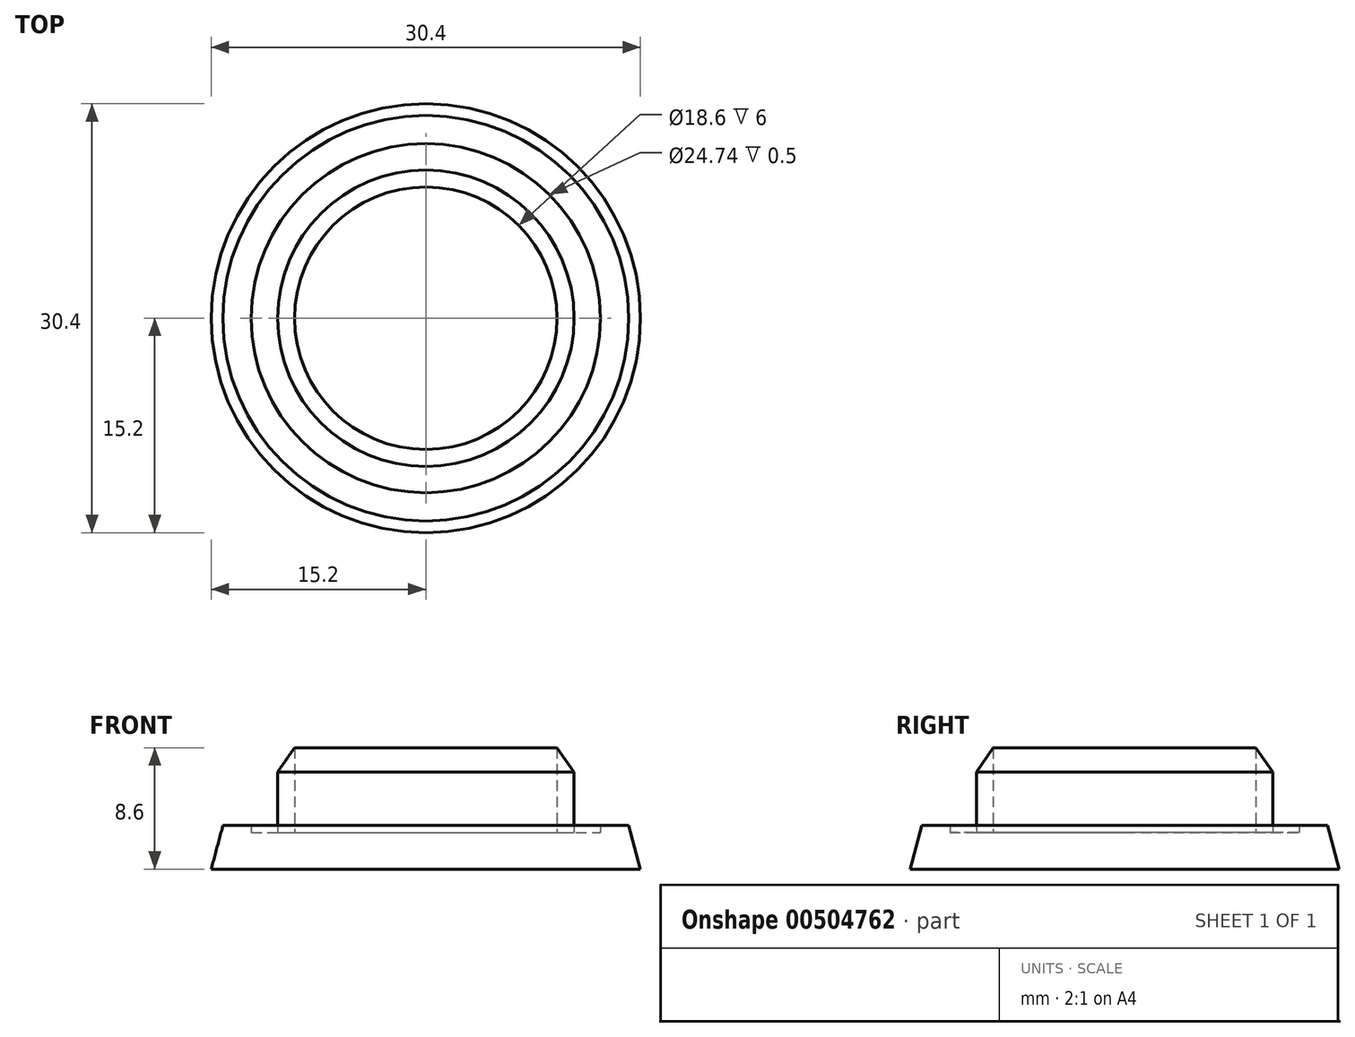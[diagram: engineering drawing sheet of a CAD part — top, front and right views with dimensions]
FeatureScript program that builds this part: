
annotation { "Feature Type Name" : "Feature", "Feature Type Description" : "" }
export const myFeature = defineFeature(function(context is Context, id is Id, definition is map)
    precondition{}
    {
        {
            var Q0;
            Q0=qCreatedBy(makeId("Front.planeOp"),FACE);
            var sketch = newSketch(context, id + "F0", { "sketchPlane" : qUnion([Q0])});
            skLineSegment(sketch, "E0", {"start": v(0, 0) * mm, "end": v(0, 9.9) * mm, "construction": true});
            skLineSegment(sketch, "E1", {"start": v(0, 0) * mm, "end": v(-15.2, 0) * mm});
            skLineSegment(sketch, "E2", {"start": v(-15.2, 0) * mm, "end": v(-14.37, 3.1) * mm});
            skLineSegment(sketch, "E3", {"start": v(-14.37, 3.1) * mm, "end": v(-12.37, 3.1) * mm});
            skLineSegment(sketch, "E4", {"start": v(-12.37, 3.1) * mm, "end": v(-12.37, 2.6) * mm});
            skLineSegment(sketch, "E5", {"start": v(-12.37, 2.6) * mm, "end": v(-10.5, 2.6) * mm});
            skLineSegment(sketch, "E6", {"start": v(-10.5, 2.6) * mm, "end": v(-10.5, 6.89) * mm});
            skLineSegment(sketch, "E7", {"start": v(-10.5, 6.89) * mm, "end": v(-9.3, 8.6) * mm});
            skLineSegment(sketch, "E8", {"start": v(-9.3, 8.6) * mm, "end": v(-9.3, 2.6) * mm});
            skLineSegment(sketch, "E9", {"start": v(-9.3, 2.6) * mm, "end": v(0, 2.6) * mm});
            skLineSegment(sketch, "E10", {"start": v(0, 2.6) * mm, "end": v(0, 0) * mm});
            skSolve(sketch);
        }
        {
            var Q0;
            Q0 = qSketchRegion(id + "F0", true);
            var Q1;
            Q1=sQuery(id+"F0.wireOp",EDGE,"E0");
            revolve(context, id + "F1", {"surfaceOperationType" : NewSurfaceOperationType.NEW, "entities" : qUnion([Q0]), "axis" : qUnion([Q1]), "revolveType" : RevolveType.FULL});
        }
    });
